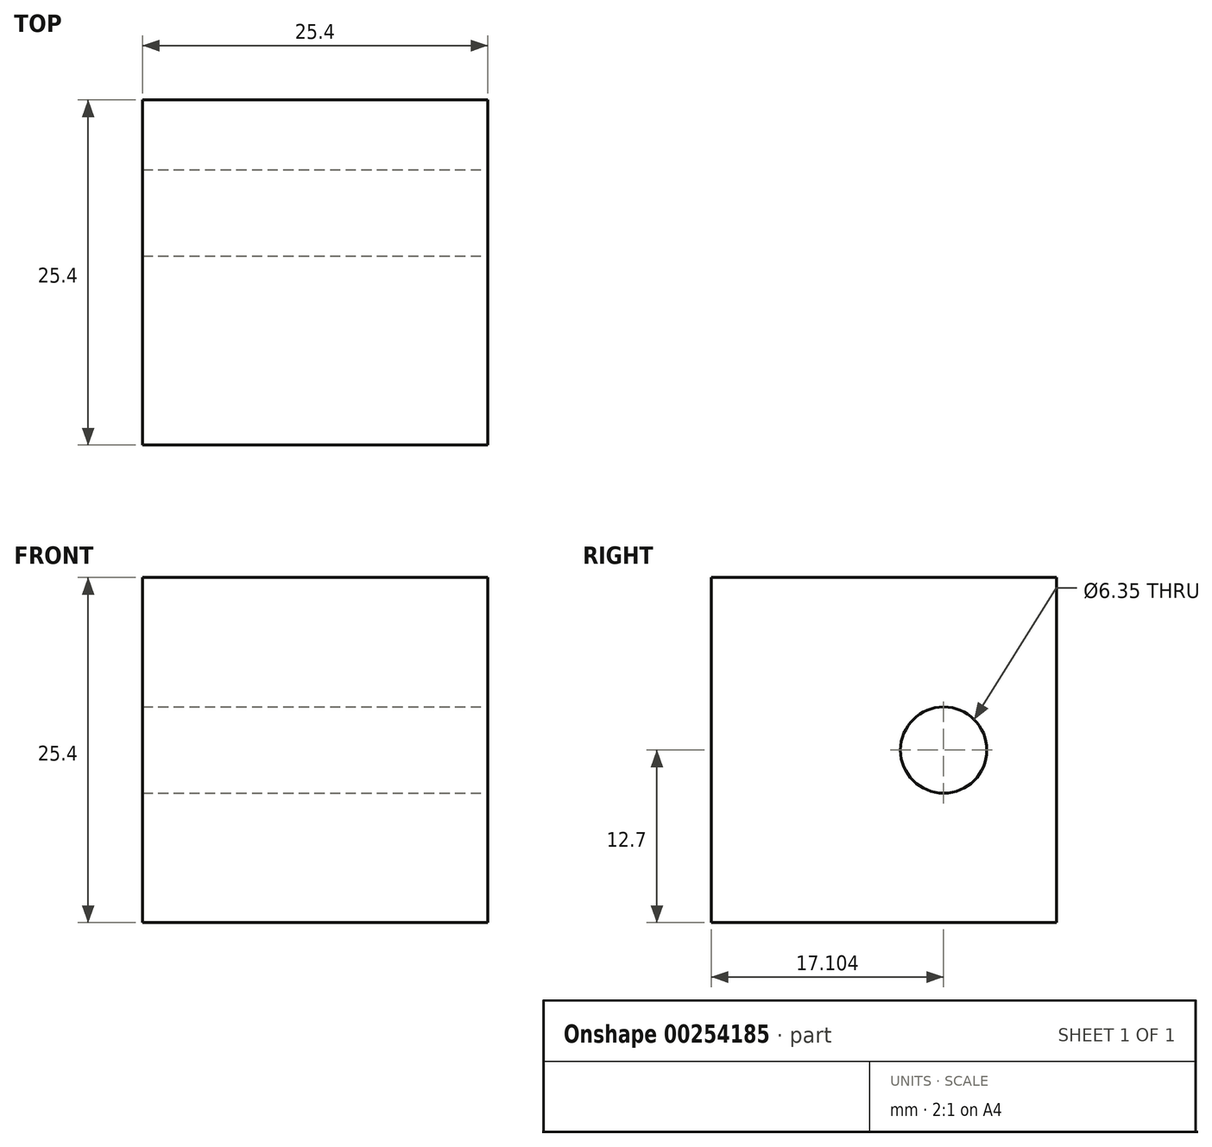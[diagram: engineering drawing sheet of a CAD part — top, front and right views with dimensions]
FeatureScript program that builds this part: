
annotation { "Feature Type Name" : "Feature", "Feature Type Description" : "" }
export const myFeature = defineFeature(function(context is Context, id is Id, definition is map)
    precondition{}
    {
        {
            var Q0;
            Q0=qCreatedBy(makeId("Front.planeOp"),FACE);
            var sketch = newSketch(context, id + "F0", { "sketchPlane" : qUnion([Q0])});
            skLineSegment(sketch, "E0.bottom", {"start": v(0, 0) * mm, "end": v(25.4, 0) * mm});
            skLineSegment(sketch, "E0.top", {"start": v(0, 25.4) * mm, "end": v(25.4, 25.4) * mm});
            skLineSegment(sketch, "E0.left", {"start": v(0, 0) * mm, "end": v(0, 25.4) * mm});
            skLineSegment(sketch, "E0.right", {"start": v(25.4, 0) * mm, "end": v(25.4, 25.4) * mm});
            skSolve(sketch);
        }
        {
            var Q0;
            Q0 = qSketchRegion(id + "F0", true);
            extrude(context, id + "F1", {"entities" : qUnion([Q0]), "depth" : 25.4 * mm});
        }
        {
            var Q0;
            Q0=makeQuery(id+"F1.opExtrude","SWEPT_FACE",FACE,{"disambiguationData":[OSD([sQuery(id+"F0.wireOp",EDGE,"E0.right")])]});
            var sketch = newSketch(context, id + "F2", { "sketchPlane" : qUnion([Q0])});
            skPoint(sketch, "E1", {"position": v(-8.3, 12.7) * mm});
            skPoint(sketch, "E1.positionSnap0", {"position": v(0, 12.7) * mm});
            skSolve(sketch);
        }
        {
            var Q0;
            Q0=sQuery(id+"F2.wireOp",VERTEX,"E1");
            var Q1;
            Q1=makeQuery(id+"F1.opExtrude","SWEPT_BODY",BODY,{"disambiguationData":[OSD([sQuery(id+"F0.wireOp",EDGE,"E0.bottom"),sQuery(id+"F0.wireOp",EDGE,"E0.top"),sQuery(id+"F0.wireOp",EDGE,"E0.left"),sQuery(id+"F0.wireOp",EDGE,"E0.right")])]});
            hole(context, id + "F3", {"style" : HoleStyle.SIMPLE, "endStyle" : HoleEndStyle.THROUGH, "holeDiameter" : 6.35 * mm, "tappedDepth" : 12.7 * mm, "tapClearance" : 3, "locations" : qUnion([Q0]), "scope" : qUnion([Q1])});
        }
    });
